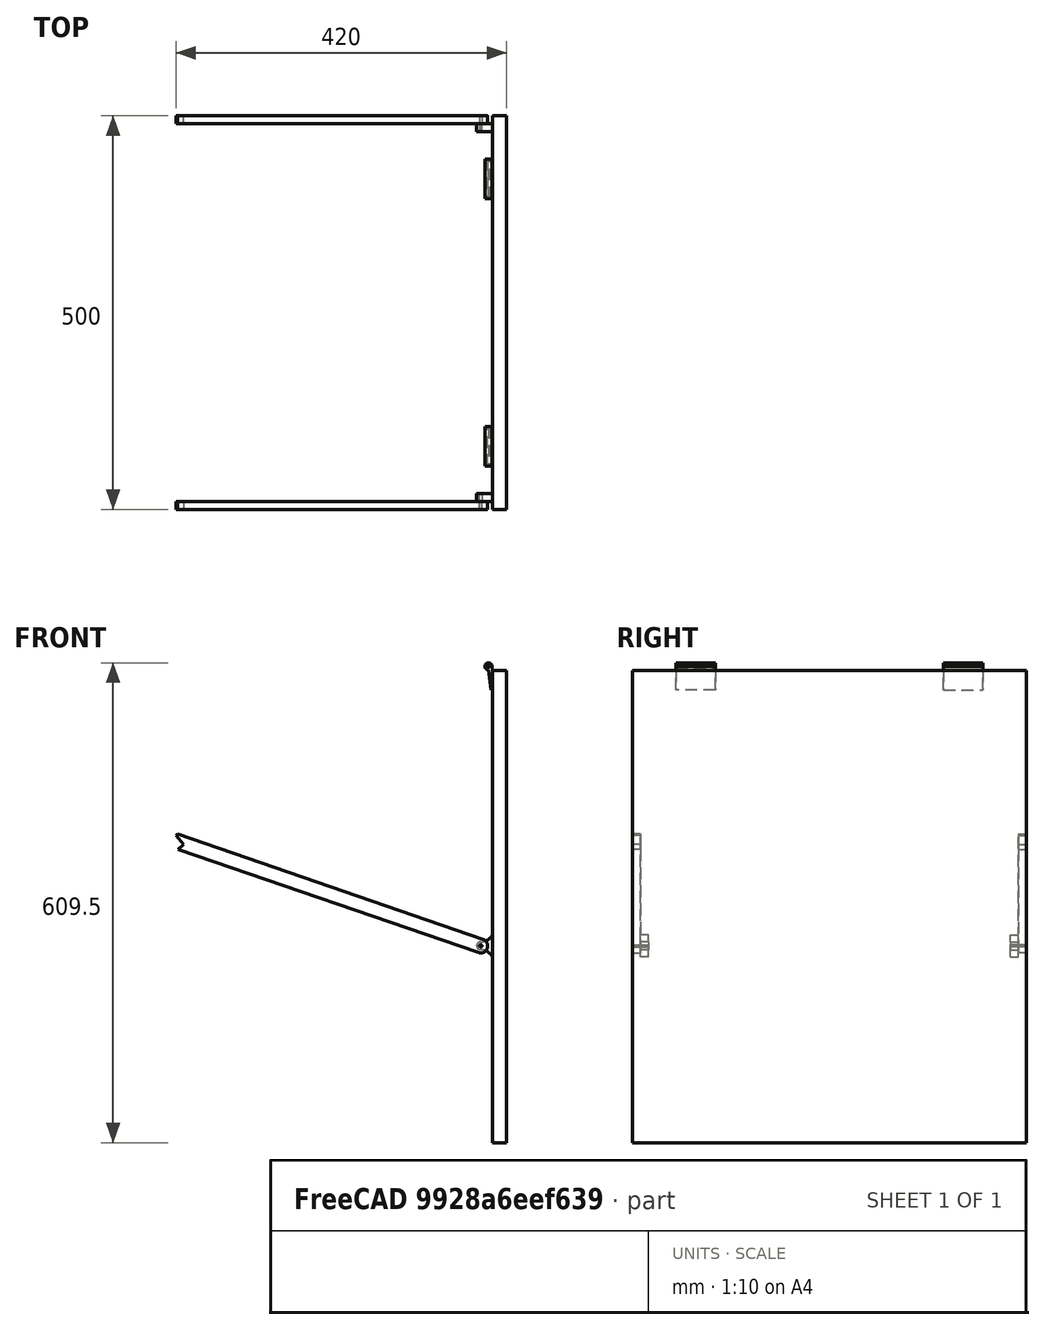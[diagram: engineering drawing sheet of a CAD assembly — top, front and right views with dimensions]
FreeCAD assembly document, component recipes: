
FREECAD ASSEMBLY — COMPONENT RECIPES ("table_jeu")

This assembly document has 2 components, labeled P0..P1 below (a component is one placed body or linked part). 1 of them carries a construction recipe — the FreeCAD feature program that regenerates the part from scratch, quoted from this document or its linked companion documents; the rest are supplied as boundary geometry only. No exploded tour is included for this assembly.
COMPONENT P0 — geometry summary ("Coffre"; no construction recipe available for this part):
  bounding box: 584.0 x 527.5 x 500.0 mm
  tessellated surface: 768 triangles
  volume: 18776364 mm^3 (12% of its bounding box)
  symmetry: mirror-symmetric across its y mid-plane
COMPONENT P1 — recipe-attached ("Lid", modeled in this document).
Construction recipe (the document's own serialized feature program — sketch geometry with constraints, then the solid features built on it; lengths are millimeters unless a unit is written):

FEATURE [Sketcher::SketchObject] Sketch002
  FullyConstrained = true
  MapMode = 5
  Placement = pos=(0,0,0) rot=(1,0,0;1.5708rad)
  Support = -> [XZ_Plane003]
  expr: Constraints[8] = Spreadsheet.plk_thic
  sketch-geometry (4):
    g0: LineSegment StartX=5 StartY=-5 StartZ=0 EndX=23 EndY=-5 EndZ=0
    g1: LineSegment StartX=23 StartY=-5 StartZ=0 EndX=23 EndY=-605 EndZ=0
    g2: LineSegment StartX=23 StartY=-605 StartZ=0 EndX=5 EndY=-605 EndZ=0
    g3: LineSegment StartX=5 StartY=-605 StartZ=0 EndX=5 EndY=-5 EndZ=0
  constraints (12):
    c: Coincident(g0,g1)
    c: Coincident(g1,g2)
    c: Coincident(g2,g3)
    c: Coincident(g3,g0)
    c: Horizontal(g0)
    c: Horizontal(g2)
    c: Vertical(g1)
    c: Vertical(g3)
    c: Distance(g0) = 18
    c: DistanceX(g-1,g0) = 5
    c: DistanceY(g0,g-1) = 5
    c: Distance(g3) = 600
FEATURE [PartDesign::Pad] Pad002
  Direction = (0,-1,-2e-16)
  Length = 500
  Length2 = 10
  Midplane = true
  Placement = pos=(0,0,0) rot=(1,0,0;1.5708rad)
  Profile = -> Sketch002
  ReferenceAxis = -> Sketch002 [N_Axis]
  Type = 0
FEATURE [Sketcher::SketchObject] Sketch003
  ExternalGeometry = -> [Pad002]
  FullyConstrained = true
  MapMode = 5
  Placement = pos=(0,-250,-5.55e-14) rot=(1,0,0;1.5708rad)
  Support = -> [Pad002]
  sketch-geometry (6):
    g0: Circle CenterX=-3.47e-14 CenterY=0 CenterZ=0 NormalX=0 NormalY=0 NormalZ=1 AngleXU=0 Radius=1.5
    g1: ArcOfCircle CenterX=-3.47e-14 CenterY=0 CenterZ=0 NormalX=0 NormalY=0 NormalZ=1 AngleXU=0 Radius=4.5 StartAngle=0 EndAngle=4.71239
    g2: LineSegment StartX=4.5 StartY=0 StartZ=0 EndX=5 EndY=-5 EndZ=0
    g3: LineSegment StartX=5 StartY=-5 StartZ=0 EndX=5 EndY=-30 EndZ=0
    g4: LineSegment StartX=5 StartY=-30 StartZ=0 EndX=3 EndY=-30 EndZ=0
    g5: LineSegment StartX=3 StartY=-30 StartZ=0 EndX=-3.46e-14 EndY=-4.5 EndZ=0
  constraints (16):
    c: Coincident(g0,g-1)
    c: Coincident(g1,g0)
    c: PointOnObject(g1,g-1)
    c: Diameter(g0) = 3
    c: Radius(g1) = 4.5
    c: Coincident(g1,g2)
    c: Coincident(g2,g-3)
    c: Coincident(g2,g3)
    c: PointOnObject(g3,g-3)
    c: Coincident(g3,g4)
    c: Horizontal(g4)
    c: Coincident(g4,g5)
    c: Coincident(g5,g1)
    c: Distance(g4) = 2
    c: Distance(g3) = 25
    c: Vertical(g0,g1)
FEATURE [PartDesign::Pad] Pad003
  BaseFeature = -> Pad002
  Direction = (0,-1,-2e-16)
  Length = 105
  Length2 = -55
  Placement = pos=(0,0,0) rot=(1,0,0;1.5708rad)
  Profile = -> Sketch003
  ReferenceAxis = -> Sketch003 [N_Axis]
  Reversed = true
  Type = 4
FEATURE [Sketcher::SketchObject] Sketch004
  ExternalGeometry = -> [Pad003]
  FullyConstrained = true
  MapMode = 5
  Placement = pos=(0,-250,-5.55e-14) rot=(1,0,0;1.5708rad)
  Support = -> [Pad003]
  sketch-geometry (6):
    g0: Circle CenterX=-10 CenterY=-355 CenterZ=0 NormalX=0 NormalY=0 NormalZ=1 AngleXU=0 Radius=1.5
    g1: ArcOfCircle CenterX=-10 CenterY=-355 CenterZ=0 NormalX=0 NormalY=0 NormalZ=1 AngleXU=0 Radius=5 StartAngle=1.5708 EndAngle=4.71239
    g2: ArcOfCircle CenterX=-10 CenterY=-377 CenterZ=0 NormalX=0 NormalY=0 NormalZ=1 AngleXU=0 Radius=17 StartAngle=0.489957 EndAngle=1.5708
    g3: LineSegment StartX=5 StartY=-369 StartZ=0 EndX=5 EndY=-341 EndZ=0
    g4: ArcOfCircle CenterX=-10 CenterY=-333 CenterZ=0 NormalX=0 NormalY=0 NormalZ=1 AngleXU=0 Radius=17 StartAngle=4.71239 EndAngle=5.79323
    g5: GeomPoint X=5 Y=-355 Z=0
  constraints (17):
    c: Coincident(g1,g0)
    c: Tangent(g1,g2) = 1.5708
    c: PointOnObject(g2,g-3)
    c: Coincident(g2,g3)
    c: Coincident(g4,g3)
    c: Coincident(g4,g1)
    c: Diameter(g0) = 3
    c: Radius(g1) = 5
    c: PointOnObject(g3,g-3)
    c: Equal(g2,g4)
    c: Vertical(g1,g1)
    c: Vertical(g1,g0)
    c: Symmetric(g3,g2,g5)
    c: Horizontal(g0,g5)
    c: DistanceY(g-3,g0) = 250
    c: DistanceX(g0,g5) = 15
    c: Radius(g4) = 17
FEATURE [PartDesign::Pad] Pad004
  BaseFeature = -> Pad003
  Direction = (0,-1,-2e-16)
  Length = 20
  Length2 = -10
  Placement = pos=(0,0,0) rot=(1,0,0;1.5708rad)
  Profile = -> Sketch004
  ReferenceAxis = -> Sketch004 [N_Axis]
  Reversed = true
  Type = 4
FEATURE [PartDesign::Mirrored] Mirrored001
  BaseFeature = -> Pad004
  MirrorPlane = -> XZ_Plane003
  Originals = -> [Pad003,Pad004]
  Placement = pos=(0,0,0) rot=(1,0,0;1.5708rad)
FEATURE [PartDesign::CoordinateSystem] LCS_4
  AttacherType = Attacher::AttachEngine3D
  MapMode = 11
  Placement = pos=(-10,-240,-355) rot=(0.57735,-0.57735,0.57735;2.0944rad)
  Support = -> [Mirrored001]
FEATURE [Sketcher::SketchObject] Sketch005
  AttachmentOffset = pos=(0,0,240) rot=(0,0,1;-0.331613rad)
  ExternalGeometry = -> [Mirrored001]
  FullyConstrained = true
  MapMode = 5
  Placement = pos=(0,-240,-5.33e-14) rot=(-0.97312,-0.162845,0.162845;4.68515rad)
  Support = -> [XZ_Plane003]
  expr: .AttachmentOffset.Rotation.Angle = Spreadsheet.leg_angle
  expr: Constraints[11] = Spreadsheet.plk_thic
  sketch-geometry (7):
    g0: Circle CenterX=106.122 CenterY=-338.915 CenterZ=0 NormalX=0 NormalY=0 NormalZ=1 AngleXU=0 Radius=1.5
    g1: ArcOfCircle CenterX=106.122 CenterY=-338.915 CenterZ=0 NormalX=0 NormalY=0 NormalZ=1 AngleXU=0 Radius=9 StartAngle=4.71239 EndAngle=7.85398
    g2: LineSegment StartX=106.122 StartY=-329.915 StartZ=0 EndX=-303.878 EndY=-329.915 EndZ=0
    g3: LineSegment StartX=-303.878 StartY=-329.915 StartZ=0 EndX=-305.378 EndY=-332.513 EndZ=0
    g4: LineSegment StartX=-305.378 StartY=-332.513 StartZ=0 EndX=-292.388 EndY=-340.013 EndZ=0
    g5: LineSegment StartX=-292.388 StartY=-340.013 StartZ=0 EndX=-296.95 EndY=-347.915 EndZ=0
    g6: LineSegment StartX=-296.95 StartY=-347.915 StartZ=0 EndX=106.122 EndY=-347.915 EndZ=0
  constraints (20):
    c: Coincident(g0,g-3)
    c: Coincident(g1,g0)
    c: Coincident(g1,g2)
    c: Horizontal(g2)
    c: Coincident(g2,g3)
    c: Coincident(g3,g4)
    c: Coincident(g4,g5)
    c: Coincident(g5,g6)
    c: Coincident(g6,g1)
    c: Horizontal(g6)
    c: Diameter(g0) = 3
    c: Diameter(g1) = 18
    c: Perpendicular(g4,g5)
    c: Distance(g4) = 15
    c: Distance(g2) = 410
    c: Vertical(g1,g1)
    c: Vertical(g1,g0)
    c: Distance(g3) = 3
    c: Angle(g3,g2) = 2.0944
    c: Angle(g4,g3) = 1.5708
FEATURE [PartDesign::Pad] Pad005
  BaseFeature = -> Mirrored001
  Direction = (0,-1,-2e-16)
  Length = 10
  Length2 = 10
  Placement = pos=(0,0,0) rot=(1,0,0;1.5708rad)
  Profile = -> Sketch005
  ReferenceAxis = -> Sketch005 [N_Axis]
  Type = 0
FEATURE [PartDesign::Body] MirroredBody
  Origin = -> Origin007
FEATURE [PartDesign::Mirrored] Mirrored002
  BaseFeature = -> Pad005
  MirrorPlane = -> XZ_Plane003
  Originals = -> [Pad005]
  Placement = pos=(0,0,0) rot=(1,0,0;1.5708rad)
FEATURE [PartDesign::Body] Body001  label="Lid001"
  Group = -> [Sketch002,Pad002,Sketch003,Pad003,Sketch004,Pad004,Mirrored001,LCS_4,Sketch005,Pad005,Mirrored002]
  Origin = -> Origin003
  Tip = -> Mirrored002
  expr: .Placement.Rotation.Angle = Spreadsheet.lid_angle
PROVENANCE & LICENSES
A FreeCAD (.FCStd) document from a public repository crawl; recipes are the document's own serialized feature recipes (and, for linked parts, companion documents' recipes).
License: mit.
